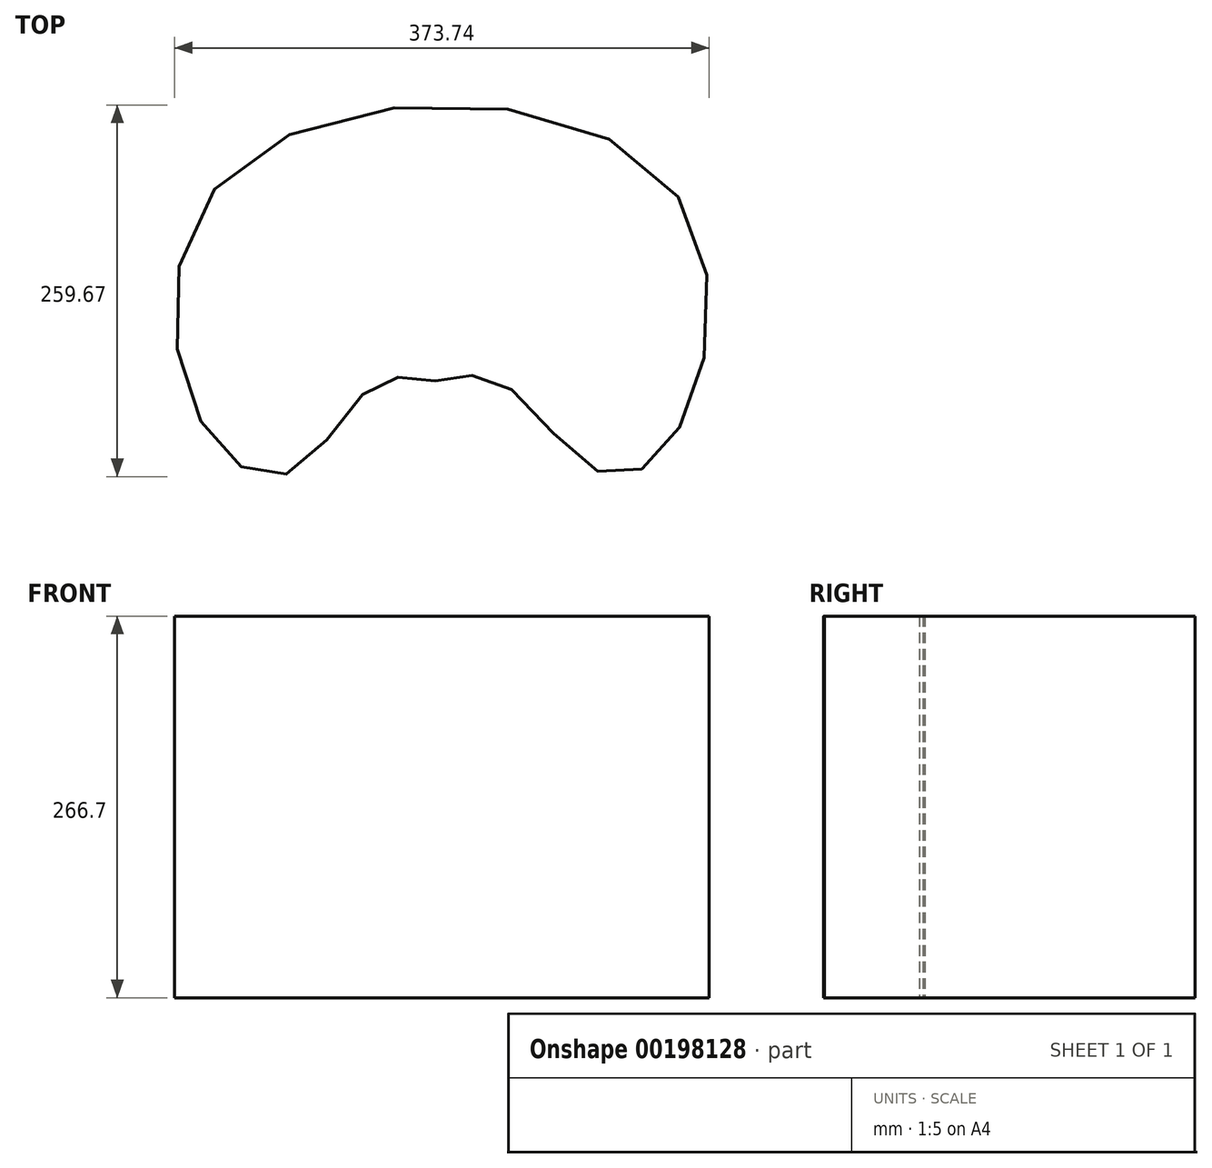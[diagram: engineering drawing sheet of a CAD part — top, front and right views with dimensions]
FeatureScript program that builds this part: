
annotation { "Feature Type Name" : "Feature", "Feature Type Description" : "" }
export const myFeature = defineFeature(function(context is Context, id is Id, definition is map)
    precondition{}
    {
        {
            var Q0;
            Q0=qCreatedBy(makeId("Top.planeOp"),FACE);
            var sketch = newSketch(context, id + "F0", { "sketchPlane" : qUnion([Q0])});
            skFitSpline(sketch, "E0.0", {"points": [v(-3.5, -28.97) * mm, v(39.07, -28.03) * mm, v(112.71, -93.18) * mm, v(170.45, -55.8) * mm, v(149.3, 119.28) * mm, v(-144.2, 119.17) * mm, v(-167.55, -56.45) * mm, v(-104.3, -93) * mm, v(-43.86, -29.86) * mm, v(-3.5, -28.97) * mm]});
            skSolve(sketch);
        }
        {
            var Q0;
            Q0=makeQuery(id+"F0.imprint","IMPRINT",FACE,{"disambiguationData":[TD([[makeQuery(id+"F0.imprint","IMPRINT",EDGE,{"derivedFrom":sQuery(id+"F0.wireOp",EDGE,"E0.0")}),1.0]])]});
            extrude(context, id + "F1", {"entities" : qUnion([Q0]), "depth" : 266.7 * mm});
        }
    });
